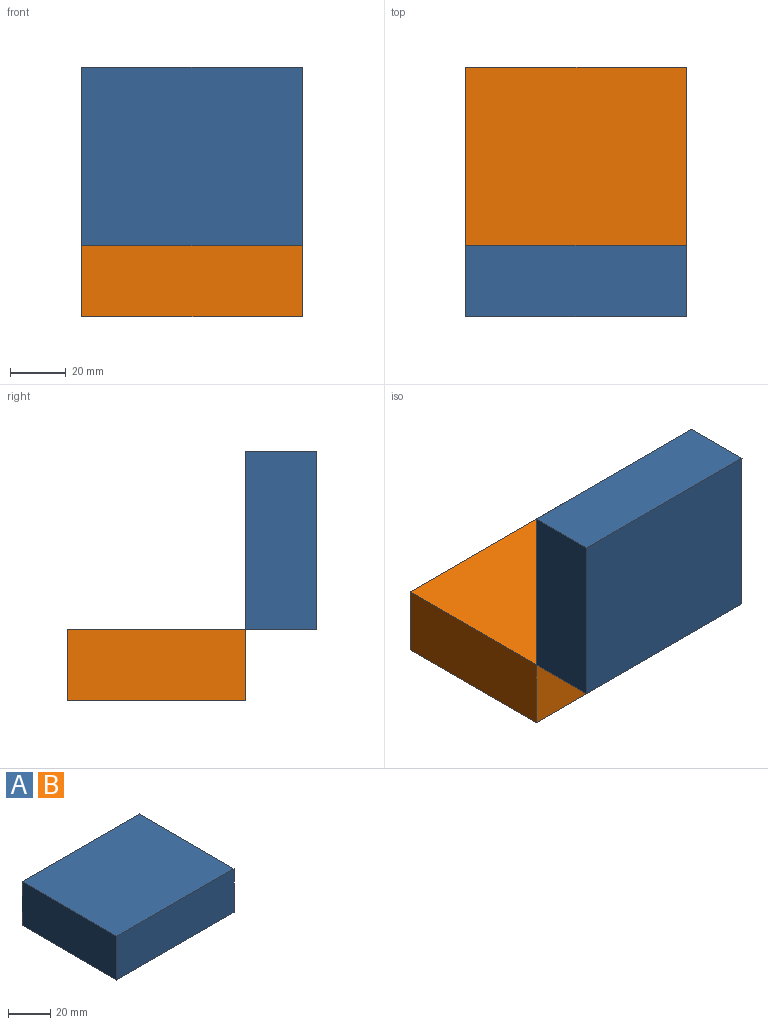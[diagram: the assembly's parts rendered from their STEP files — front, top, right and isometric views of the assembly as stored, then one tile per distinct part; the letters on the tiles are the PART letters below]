
ASSEMBLY  parts=2 mates=1
PART A: 6 faces, bbox 78.7x63.8x25.4 mm
  f0: plane 78.72x25.4mm, normal (0,1,0), area 1999.4mm2, adj f1,f3,f4,f5
  f1: plane 63.84x25.4mm, normal (-1,0,0), area 1621.4mm2, adj f0,f2,f4,f5
  f2: plane 78.72x25.4mm, normal (0,-1,0), area 1999.4mm2, adj f1,f3,f4,f5
  f3: plane 63.84x25.4mm, normal (1,0,0), area 1621.4mm2, adj f0,f2,f4,f5
  f4: plane 78.72x63.84mm, normal (0,0,1), area 5024.9mm2, adj f0,f1,f2,f3
  f5: plane 78.72x63.84mm, normal (0,0,-1), area 5024.9mm2, adj f0,f1,f2,f3
PART B: same geometry as A
PLACE A rot(axis=(1,0,0),90deg) t=(-20.4,-85.58,56.12)mm
PLACE B t=(-20.4,-50.53,-4.33)mm
MATE fastened A.f2 <-> B.f4  axis (0,0,-1) through (-17.6,-85.58,21.07)mm
